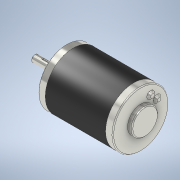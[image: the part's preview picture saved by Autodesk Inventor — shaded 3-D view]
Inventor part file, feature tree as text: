
AUTODESK INVENTOR PART (.ipt)
format: ipt  version: 2020 (Build 240168000, 168)  size: 183,808 bytes
history: native  units: in
note: dims shown in document units (in); Inventor stores cm internally (conversion verified against a paired STEP export)
features: chamfer x1
ambient origin geometry x8: Origin, YZ Plane, XZ Plane, XY Plane, X Axis, Y Axis, Z Axis, Center Point
bodies: Solid1 (feature_tree)
feature tree (1):
  chamfer  "Chamfer3"  [1 undecoded]
note: 1 required parameter value undecoded (feature->parameter linkage not recoverable at this tier; creation-order binding heuristic only, values carry confidence <= 0.55)
